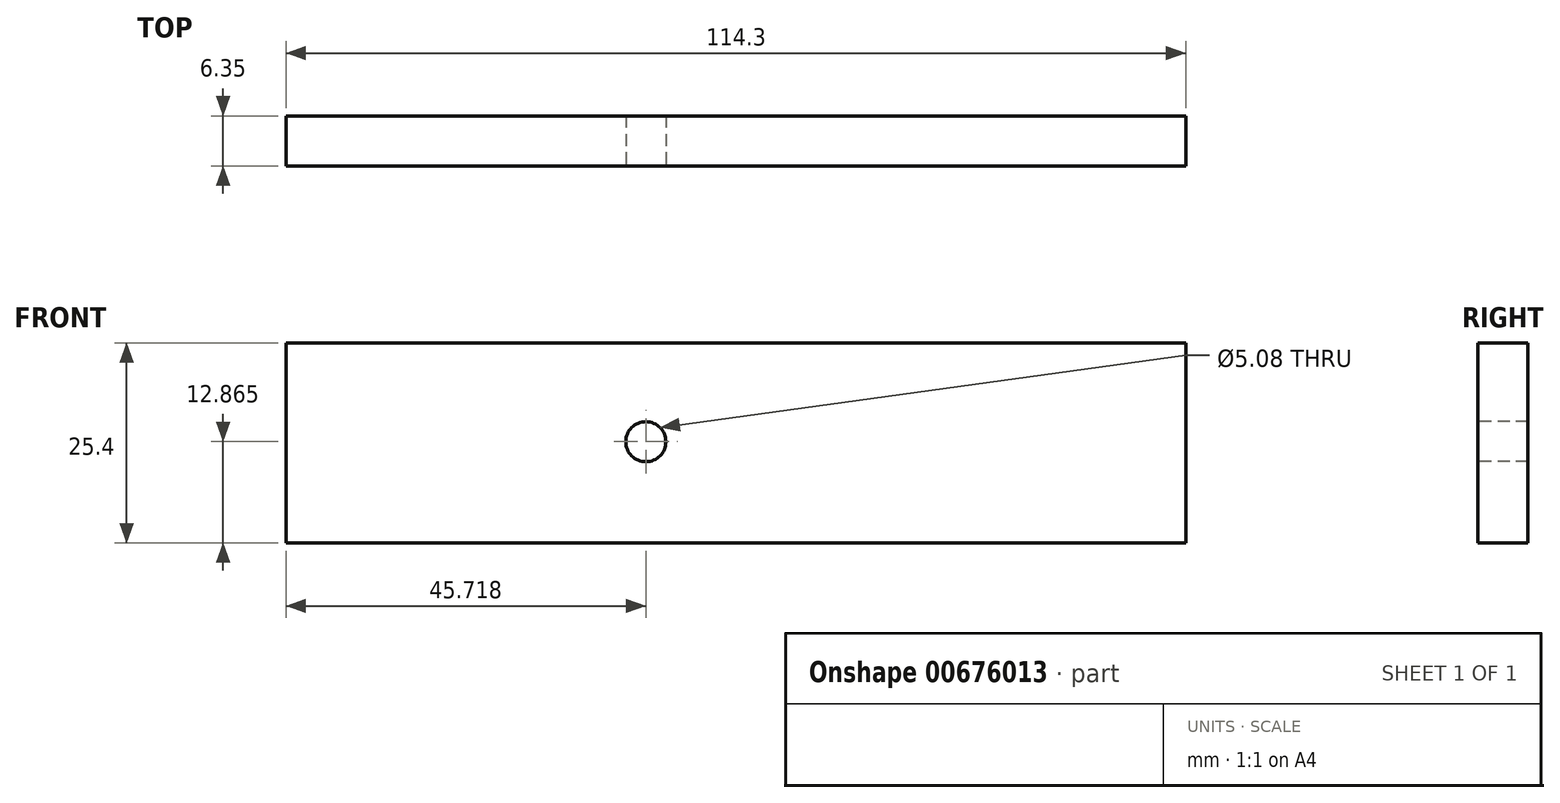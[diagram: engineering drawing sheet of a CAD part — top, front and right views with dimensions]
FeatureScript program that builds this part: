
annotation { "Feature Type Name" : "Feature", "Feature Type Description" : "" }
export const myFeature = defineFeature(function(context is Context, id is Id, definition is map)
    precondition{}
    {
        {
            var Q0;
            Q0=qCreatedBy(makeId("Front.planeOp"),FACE);
            var sketch = newSketch(context, id + "F0", { "sketchPlane" : qUnion([Q0])});
            skLineSegment(sketch, "E0.bottom", {"start": v(-92.85, 28.7) * mm, "end": v(21.45, 28.7) * mm});
            skLineSegment(sketch, "E0.top", {"start": v(-92.85, 3.3) * mm, "end": v(21.45, 3.3) * mm});
            skLineSegment(sketch, "E0.left", {"start": v(-92.85, 28.7) * mm, "end": v(-92.85, 3.3) * mm});
            skLineSegment(sketch, "E0.right", {"start": v(21.45, 28.7) * mm, "end": v(21.45, 3.3) * mm});
            skSolve(sketch);
        }
        {
            var Q0;
            Q0 = qSketchRegion(id + "F0", true);
            extrude(context, id + "F1", {"entities" : qUnion([Q0]), "depth" : 6.35 * mm, "offsetDistance" : 25.4 * mm});
        }
        {
            var Q0;
            Q0=makeQuery(id+"F1.opExtrude","CAP_FACE",FACE,{"disambiguationData":[OSD([sQuery(id+"F0.wireOp",EDGE,"E0.bottom"),sQuery(id+"F0.wireOp",EDGE,"E0.top"),sQuery(id+"F0.wireOp",EDGE,"E0.left"),sQuery(id+"F0.wireOp",EDGE,"E0.right")])],"isStart":false});
            var sketch = newSketch(context, id + "F2", { "sketchPlane" : qUnion([Q0])});
            skCircle(sketch, "E1", {"center": v(-47.13, 16.16) * mm, "radius": 2.54 * mm});
            skSolve(sketch);
        }
        {
            var Q0;
            Q0=sQuery(id+"F2.wireOp",VERTEX,"E1.center");
            var Q1;
            Q1=makeQuery(id+"F1.opExtrude","SWEPT_BODY",BODY,{"disambiguationData":[OSD([sQuery(id+"F0.wireOp",EDGE,"E0.bottom"),sQuery(id+"F0.wireOp",EDGE,"E0.top"),sQuery(id+"F0.wireOp",EDGE,"E0.left"),sQuery(id+"F0.wireOp",EDGE,"E0.right")])]});
            hole(context, id + "F3", {"style" : HoleStyle.SIMPLE, "endStyle" : HoleEndStyle.THROUGH, "holeDiameter" : 5.08 * mm, "majorDiameter" : 6.35 * mm, "isTappedThrough" : true, "tappedDepth" : 12.7 * mm, "tapClearance" : 3, "locations" : qUnion([Q0]), "scope" : qUnion([Q1])});
        }
    });
